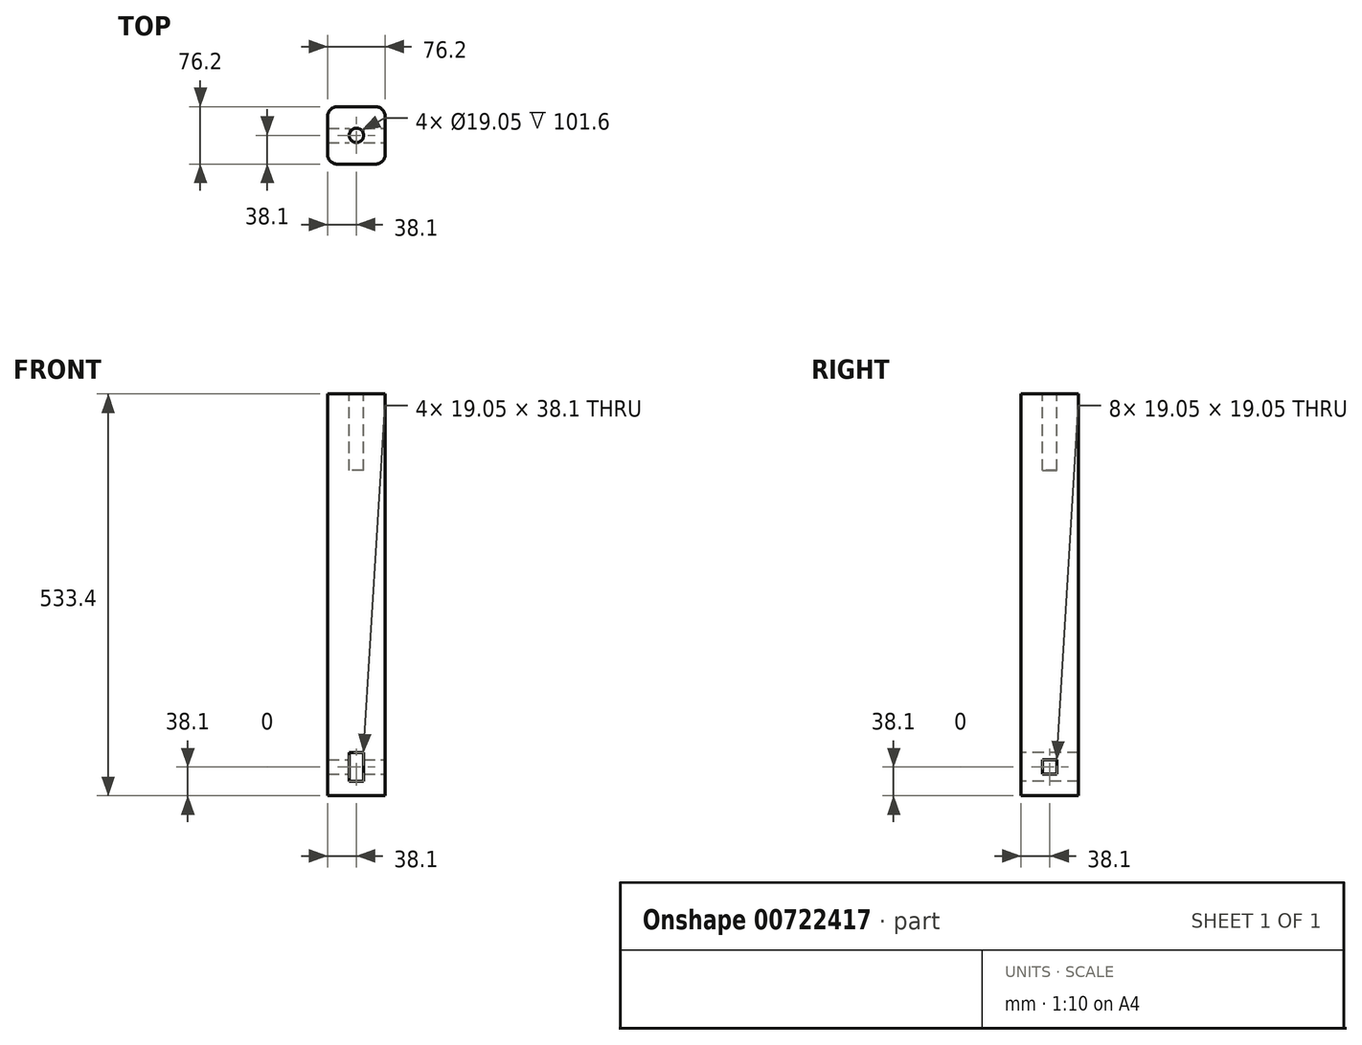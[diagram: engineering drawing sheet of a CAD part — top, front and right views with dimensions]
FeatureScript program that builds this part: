
annotation { "Feature Type Name" : "Feature", "Feature Type Description" : "" }
export const myFeature = defineFeature(function(context is Context, id is Id, definition is map)
    precondition{}
    {
        {
            var Q0;
            Q0=qCreatedBy(makeId("Top.planeOp"),FACE);
            var sketch = newSketch(context, id + "F0", { "sketchPlane" : qUnion([Q0])});
            skLineSegment(sketch, "E0.bottom", {"start": v(38.1, -38.1) * mm, "end": v(-38.1, -38.1) * mm});
            skLineSegment(sketch, "E0.top", {"start": v(38.1, 38.1) * mm, "end": v(-38.1, 38.1) * mm});
            skLineSegment(sketch, "E0.left", {"start": v(38.1, -38.1) * mm, "end": v(38.1, 38.1) * mm});
            skLineSegment(sketch, "E0.right", {"start": v(-38.1, -38.1) * mm, "end": v(-38.1, 38.1) * mm});
            skPoint(sketch, "E0.middle", {"position": v(0, 0) * mm});
            skSolve(sketch);
        }
        {
            var Q0;
            Q0=makeQuery(id+"F0.imprint","IMPRINT",FACE,{"disambiguationData":[TD([[makeQuery(id+"F0.imprint","IMPRINT",EDGE,{"derivedFrom":sQuery(id+"F0.wireOp",EDGE,"E0.bottom")}),-1.0]])]});
            extrude(context, id + "F1", {"entities" : qUnion([Q0]), "depth" : 533.4 * mm, "offsetDistance" : 25.4 * mm});
        }
        {
            var Q0;
            Q0=makeQuery(id+"F1.opExtrude","CAP_FACE",FACE,{"disambiguationData":[OSD([sQuery(id+"F0.wireOp",EDGE,"E0.bottom"),sQuery(id+"F0.wireOp",EDGE,"E0.top"),sQuery(id+"F0.wireOp",EDGE,"E0.left"),sQuery(id+"F0.wireOp",EDGE,"E0.right")])],"isStart":false});
            var sketch = newSketch(context, id + "F2", { "sketchPlane" : qUnion([Q0])});
            skCircle(sketch, "E1", {"center": v(0, 0) * mm, "radius": 9.53 * mm});
            skSolve(sketch);
        }
        {
            var Q0;
            Q0=makeQuery(id+"F2.imprint","IMPRINT",FACE,{"disambiguationData":[TD([[makeQuery(id+"F2.imprint","IMPRINT",EDGE,{"derivedFrom":sQuery(id+"F2.wireOp",EDGE,"E1")}),1.0]])]});
            extrude(context, id + "F3", {"entities" : qUnion([Q0]), "operationType" : NewBodyOperationType.REMOVE, "oppositeDirection" : true, "depth" : 101.6 * mm, "offsetDistance" : 25.4 * mm});
        }
        {
            var Q0;
            Q0=makeQuery(id+"F1.opExtrude","SWEPT_FACE",FACE,{"disambiguationData":[OSD([sQuery(id+"F0.wireOp",EDGE,"E0.bottom")])]});
            var sketch = newSketch(context, id + "F4", { "sketchPlane" : qUnion([Q0])});
            skLineSegment(sketch, "E2.bottom", {"start": v(9.52, 19.05) * mm, "end": v(-9.53, 19.05) * mm});
            skLineSegment(sketch, "E2.top", {"start": v(9.52, 57.15) * mm, "end": v(-9.53, 57.15) * mm});
            skLineSegment(sketch, "E2.left", {"start": v(9.52, 19.05) * mm, "end": v(9.52, 57.15) * mm});
            skLineSegment(sketch, "E2.right", {"start": v(-9.53, 19.05) * mm, "end": v(-9.53, 57.15) * mm});
            skPoint(sketch, "E2.middle", {"position": v(0, 38.1) * mm});
            skSolve(sketch);
        }
        {
            var Q0;
            Q0=makeQuery(id+"F4.imprint","IMPRINT",FACE,{"disambiguationData":[TD([[makeQuery(id+"F4.imprint","IMPRINT",EDGE,{"derivedFrom":sQuery(id+"F4.wireOp",EDGE,"E2.bottom")}),-1.0]])]});
            extrude(context, id + "F5", {"entities" : qUnion([Q0]), "operationType" : NewBodyOperationType.REMOVE, "endBound" : BoundingType.UP_TO_NEXT, "oppositeDirection" : true, "depth" : 25.4 * mm, "offsetDistance" : 25.4 * mm});
        }
        {
            var Q0;
            Q0=makeQuery(id+"F1.opExtrude","SWEPT_FACE",FACE,{"disambiguationData":[OSD([sQuery(id+"F0.wireOp",EDGE,"E0.left")])]});
            var sketch = newSketch(context, id + "F6", { "sketchPlane" : qUnion([Q0])});
            skLineSegment(sketch, "E3.bottom", {"start": v(9.52, 28.57) * mm, "end": v(-9.53, 28.57) * mm});
            skLineSegment(sketch, "E3.top", {"start": v(9.52, 47.62) * mm, "end": v(-9.53, 47.62) * mm});
            skLineSegment(sketch, "E3.left", {"start": v(9.52, 28.57) * mm, "end": v(9.52, 47.62) * mm});
            skLineSegment(sketch, "E3.right", {"start": v(-9.53, 28.57) * mm, "end": v(-9.53, 47.62) * mm});
            skPoint(sketch, "E3.middle", {"position": v(0, 38.1) * mm});
            skSolve(sketch);
        }
        {
            var Q0;
            Q0=makeQuery(id+"F6.imprint","IMPRINT",FACE,{"disambiguationData":[TD([[makeQuery(id+"F6.imprint","IMPRINT",EDGE,{"derivedFrom":sQuery(id+"F6.wireOp",EDGE,"E3.bottom")}),-1.0]])]});
            extrude(context, id + "F7", {"entities" : qUnion([Q0]), "operationType" : NewBodyOperationType.REMOVE, "endBound" : BoundingType.THROUGH_ALL, "oppositeDirection" : true, "depth" : 25.4 * mm, "offsetDistance" : 25.4 * mm});
        }
        {
            var Q0;
            Q0=makeQuery(id+"F1.opExtrude","SWEPT_EDGE",EDGE,{"disambiguationData":[OSD([sQuery(id+"F0.wireOp",EDGE,"E0.bottom"),sQuery(id+"F0.wireOp",EDGE,"E0.right")])]});
            var Q1;
            Q1=makeQuery(id+"F1.opExtrude","SWEPT_EDGE",EDGE,{"disambiguationData":[OSD([sQuery(id+"F0.wireOp",EDGE,"E0.bottom"),sQuery(id+"F0.wireOp",EDGE,"E0.left")])]});
            var Q2;
            Q2=makeQuery(id+"F1.opExtrude","SWEPT_EDGE",EDGE,{"disambiguationData":[OSD([sQuery(id+"F0.wireOp",EDGE,"E0.top"),sQuery(id+"F0.wireOp",EDGE,"E0.left")])]});
            var Q3;
            Q3=makeQuery(id+"F1.opExtrude","SWEPT_EDGE",EDGE,{"disambiguationData":[OSD([sQuery(id+"F0.wireOp",EDGE,"E0.top"),sQuery(id+"F0.wireOp",EDGE,"E0.right")])]});
            fillet(context, id + "F8", {"entities" : qUnion([Q0, Q1, Q2, Q3]), "radius" : 12.7 * mm, "tangentPropagation" : true, "allowEdgeOverflow" : false});
        }
    });
